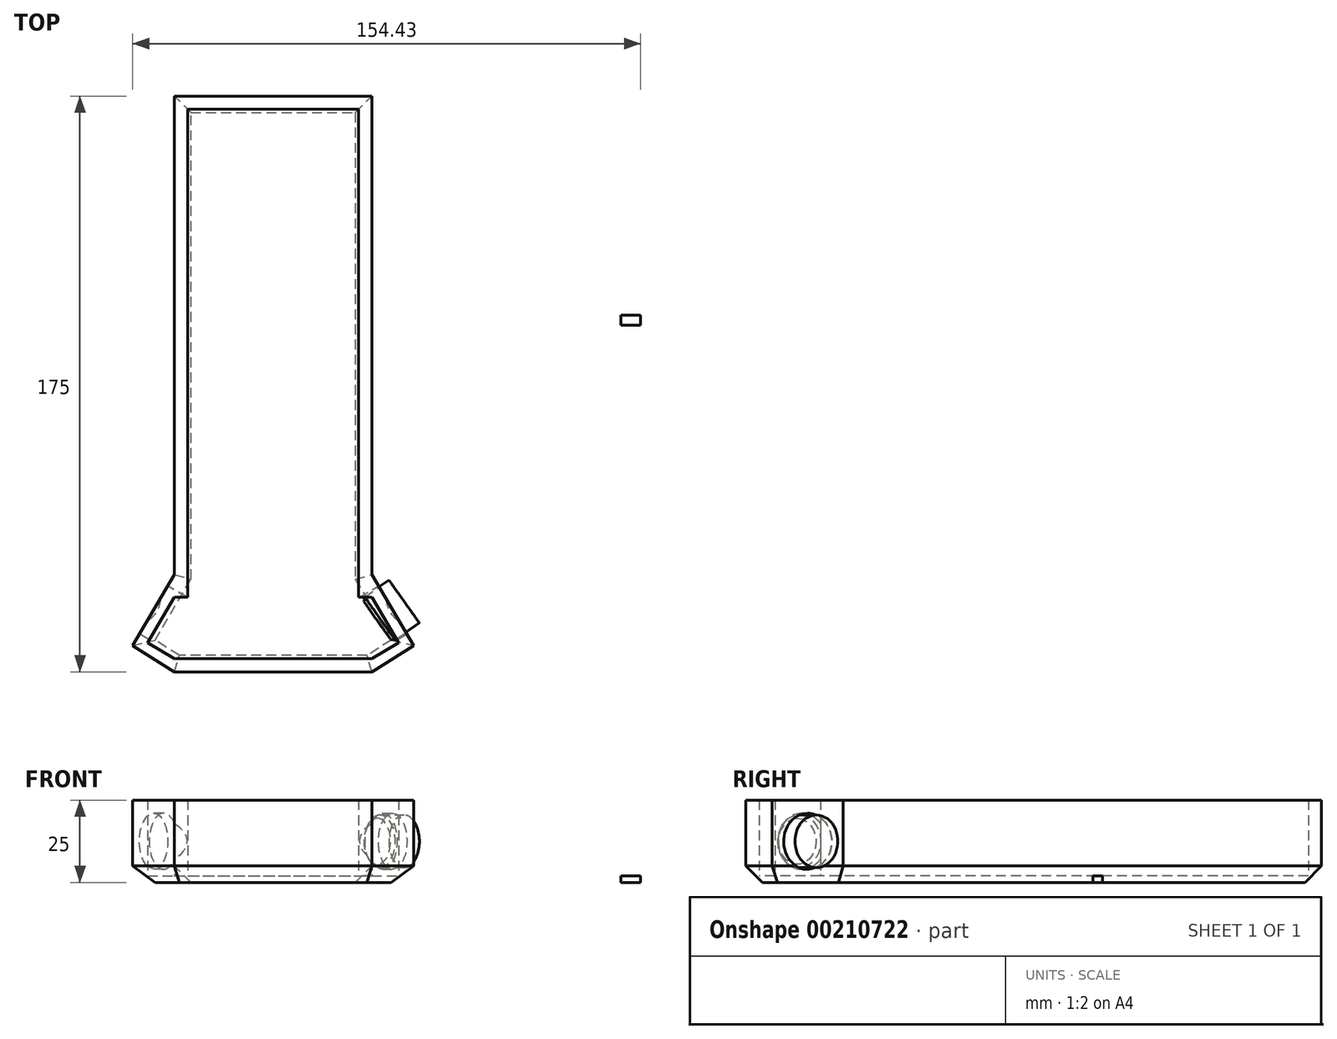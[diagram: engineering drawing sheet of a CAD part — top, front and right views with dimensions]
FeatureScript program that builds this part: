
annotation { "Feature Type Name" : "Feature", "Feature Type Description" : "" }
export const myFeature = defineFeature(function(context is Context, id is Id, definition is map)
    precondition{}
    {
        {
            var Q0;
            Q0=qCreatedBy(makeId("Top.planeOp"),FACE);
            var sketch = newSketch(context, id + "F0", { "sketchPlane" : qUnion([Q0])});
            skLineSegment(sketch, "E0.top", {"start": v(-60, -53.6) * mm, "end": v(0, -53.6) * mm});
            skLineSegment(sketch, "E0.left", {"start": v(-60, 121.4) * mm, "end": v(-60, -30.92) * mm});
            skLineSegment(sketch, "E0.right", {"start": v(0, 121.4) * mm, "end": v(0, -30.92) * mm});
            skLineSegment(sketch, "E1", {"start": v(-60, 121.4) * mm, "end": v(0, 121.4) * mm});
            skLineSegment(sketch, "E2.bottom", {"start": v(-56, 117.4) * mm, "end": v(-4, 117.4) * mm});
            skLineSegment(sketch, "E2.top", {"start": v(-56, -49.6) * mm, "end": v(-4, -49.6) * mm});
            skLineSegment(sketch, "E2.left", {"start": v(-56, 117.4) * mm, "end": v(-56, -30.92) * mm});
            skLineSegment(sketch, "E2.right", {"start": v(-4, 117.4) * mm, "end": v(-4, -30.92) * mm});
            skLineSegment(sketch, "E3", {"start": v(0, -53.6) * mm, "end": v(12.7, -45.6) * mm});
            skLineSegment(sketch, "E4", {"start": v(12.7, -45.6) * mm, "end": v(0, -24.06) * mm});
            skLineSegment(sketch, "E5", {"start": v(11.17, -43.01) * mm, "end": v(0, -49.6) * mm});
            skPoint(sketch, "E5.endSnap0", {"position": v(6.35, -49.6) * mm});
            skLineSegment(sketch, "E6", {"start": v(-4, -49.6) * mm, "end": v(0, -49.6) * mm});
            skLineSegment(sketch, "E7", {"start": v(3, -29.15) * mm, "end": v(0, -30.92) * mm});
            skLineSegment(sketch, "E8", {"start": v(0, -30.92) * mm, "end": v(-4, -30.92) * mm});
            skPoint(sketch, "E9.MirrorCS.end.orphan", {"position": v(-60, -24.06) * mm});
            skPoint(sketch, "E9.MirrorCS.start.orphan", {"position": v(-72.7, -45.6) * mm});
            skPoint(sketch, "E10.MirrorCS.start.orphan", {"position": v(-60, -53.6) * mm});
            skPoint(sketch, "E11.end.orphan", {"position": v(-30, -49.6) * mm});
            skPoint(sketch, "E11.start.orphan", {"position": v(-30, 117.4) * mm});
            skCircle(sketch, "E12", {"center": v(130.43, 55.25) * mm, "radius": 8 * mm});
            skLineSegment(sketch, "E13", {"start": v(138.43, 55.25) * mm, "end": v(122.43, 55.25) * mm});
            skLineSegment(sketch, "E14.MirrorCS", {"start": v(-63, -29.15) * mm, "end": v(-60, -30.92) * mm});
            skLineSegment(sketch, "E15.MirrorCS", {"start": v(-72.7, -45.6) * mm, "end": v(-60, -24.06) * mm});
            skLineSegment(sketch, "E16.MirrorCS", {"start": v(-71.17, -43.01) * mm, "end": v(-60, -49.6) * mm});
            skLineSegment(sketch, "E17.MirrorCS", {"start": v(-60, -53.6) * mm, "end": v(-72.7, -45.6) * mm});
            skLineSegment(sketch, "E18.MirrorCS", {"start": v(-60, -30.92) * mm, "end": v(-56, -30.92) * mm});
            skLineSegment(sketch, "E19.trimOffspring", {"start": v(0, -49.6) * mm, "end": v(0, -53.6) * mm});
            skLineSegment(sketch, "E20", {"start": v(-60, -49.6) * mm, "end": v(-56, -49.6) * mm});
            skLineSegment(sketch, "E21.trimOffspring", {"start": v(-60, -49.6) * mm, "end": v(-60, -53.6) * mm});
            skLineSegment(sketch, "E22", {"start": v(-60, -30.92) * mm, "end": v(-68.17, -44.78) * mm});
            skLineSegment(sketch, "E23", {"start": v(0, -30.92) * mm, "end": v(8.17, -44.78) * mm});
            skLineSegment(sketch, "E24", {"start": v(-60, -30.92) * mm, "end": v(-60, -49.6) * mm});
            skLineSegment(sketch, "E25", {"start": v(-56, -49.6) * mm, "end": v(-56, -30.92) * mm});
            skLineSegment(sketch, "E26", {"start": v(-4, -49.6) * mm, "end": v(-4, -30.92) * mm});
            skLineSegment(sketch, "E27", {"start": v(0, -49.6) * mm, "end": v(0, -30.92) * mm});
            skPoint(sketch, "E28.start.orphan", {"position": v(-30, 9.4) * mm});
            skPoint(sketch, "E29.orphan", {"position": v(-60, 165.4) * mm});
            skLineSegment(sketch, "E30.bottom", {"start": v(75.74, 54.83) * mm, "end": v(81.74, 54.83) * mm});
            skLineSegment(sketch, "E30.top", {"start": v(75.74, 51.83) * mm, "end": v(81.74, 51.83) * mm});
            skLineSegment(sketch, "E30.left", {"start": v(75.74, 54.83) * mm, "end": v(75.74, 51.83) * mm});
            skLineSegment(sketch, "E30.right", {"start": v(81.74, 54.83) * mm, "end": v(81.74, 51.83) * mm});
            skSolve(sketch);
        }
        {
            var Q0;
            {var subQ2=sQuery(id+"F0.wireOp",EDGE,"E0.top");Q0=makeQuery(id+"F0.imprint","IMPRINT",FACE,{"disambiguationData":[TD([[makeQuery(id+"F0.imprint","IMPRINT",EDGE,{"derivedFrom":subQ2}),1.0]])]});}
            var Q1;
            {var subQ0=sQuery(id+"F0.wireOp",EDGE,"E17.MirrorCS");Q1=makeQuery(id+"F0.imprint","IMPRINT",FACE,{"disambiguationData":[TD([[makeQuery(id+"F0.imprint","IMPRINT",EDGE,{"derivedFrom":subQ0}),-1.0]])]});}
            var Q2;
            {var subQ0=sQuery(id+"F0.wireOp",EDGE,"E14.MirrorCS");Q2=makeQuery(id+"F0.imprint","IMPRINT",FACE,{"disambiguationData":[TD([[makeQuery(id+"F0.imprint","IMPRINT",EDGE,{"derivedFrom":subQ0}),1.0]])]});}
            var Q3;
            {var subQ0=sQuery(id+"F0.wireOp",EDGE,"E14.MirrorCS");Q3=makeQuery(id+"F0.imprint","IMPRINT",FACE,{"disambiguationData":[TD([[makeQuery(id+"F0.imprint","IMPRINT",EDGE,{"derivedFrom":subQ0}),-1.0]])]});}
            var Q4;
            {var subQ4=sQuery(id+"F0.wireOp",EDGE,"E1");Q4=makeQuery(id+"F0.imprint","IMPRINT",FACE,{"disambiguationData":[TD([[makeQuery(id+"F0.imprint","IMPRINT",EDGE,{"derivedFrom":subQ4}),-1.0]])]});}
            var Q5;
            {var subQ0=sQuery(id+"F0.wireOp",EDGE,"E7");Q5=makeQuery(id+"F0.imprint","IMPRINT",FACE,{"disambiguationData":[TD([[makeQuery(id+"F0.imprint","IMPRINT",EDGE,{"derivedFrom":subQ0}),-1.0]])]});}
            var Q6;
            {var subQ3=sQuery(id+"F0.wireOp",EDGE,"E7");Q6=makeQuery(id+"F0.imprint","IMPRINT",FACE,{"disambiguationData":[TD([[makeQuery(id+"F0.imprint","IMPRINT",EDGE,{"derivedFrom":subQ3}),1.0]])]});}
            var Q7;
            {var subQ5=sQuery(id+"F0.wireOp",EDGE,"E3");Q7=makeQuery(id+"F0.imprint","IMPRINT",FACE,{"disambiguationData":[TD([[makeQuery(id+"F0.imprint","IMPRINT",EDGE,{"derivedFrom":subQ5}),1.0]])]});}
            extrude(context, id + "F1", {"entities" : qUnion([Q0, Q1, Q2, Q3, Q4, Q5, Q6, Q7]), "depth" : 25 * mm});
        }
        {
            var Q0;
            Q0=makeQuery(id+"F0.imprint","IMPRINT",FACE,{"disambiguationData":[TD([[makeQuery(id+"F0.imprint","IMPRINT",EDGE,{"derivedFrom":sQuery(id+"F0.wireOp",EDGE,"E2.bottom")}),-1.0]])]});
            var Q1;
            {var subQ2=sQuery(id+"F0.wireOp",EDGE,"E23");Q1=makeQuery(id+"F0.imprint","IMPRINT",FACE,{"disambiguationData":[TD([[makeQuery(id+"F0.imprint","IMPRINT",EDGE,{"derivedFrom":subQ2}),-1.0]])]});}
            var Q2;
            Q2=makeQuery(id+"F0.imprint","IMPRINT",FACE,{"disambiguationData":[TD([[makeQuery(id+"F0.imprint","IMPRINT",EDGE,{"derivedFrom":sQuery(id+"F0.wireOp",EDGE,"E6")}),1.0]])]});
            var Q3;
            {var subQ2=sQuery(id+"F0.wireOp",EDGE,"E22");Q3=makeQuery(id+"F0.imprint","IMPRINT",FACE,{"disambiguationData":[TD([[makeQuery(id+"F0.imprint","IMPRINT",EDGE,{"derivedFrom":subQ2}),1.0]])]});}
            var Q4;
            Q4=makeQuery(id+"F0.imprint","IMPRINT",FACE,{"disambiguationData":[TD([[makeQuery(id+"F0.imprint","IMPRINT",EDGE,{"derivedFrom":sQuery(id+"F0.wireOp",EDGE,"E18.MirrorCS")}),-1.0]])]});
            extrude(context, id + "F2", {"entities" : qUnion([Q0, Q1, Q2, Q3, Q4]), "operationType" : NewBodyOperationType.ADD, "depth" : 2 * mm});
        }
        {
            var Q0;
            Q0=makeQuery(id+"F1.opExtrude","SWEPT_FACE",FACE,{"disambiguationData":[OSD([sQuery(id+"F0.wireOp",EDGE,"E4")])]});
            var sketch = newSketch(context, id + "F3", { "sketchPlane" : qUnion([Q0])});
            skCircle(sketch, "E31", {"center": v(-33.23, 12.5) * mm, "radius": 8.5 * mm});
            skPoint(sketch, "E31.centerSnap0", {"position": v(-20.73, 12.5) * mm});
            skPoint(sketch, "E31.centerSnap1", {"position": v(-33.23, 0) * mm});
            skLineSegment(sketch, "E32", {"start": v(-33.23, 4) * mm, "end": v(-33.23, 21) * mm});
            skSolve(sketch);
        }
        {
            var Q0;
            Q0 = qSketchRegion(id + "F3", true);
            extrude(context, id + "F4", {"entities" : qUnion([Q0]), "operationType" : NewBodyOperationType.REMOVE, "oppositeDirection" : true, "depth" : 8 * mm});
        }
        {
            var Q0;
            {var subQ0=sQuery(id+"F0.wireOp",EDGE,"E13");Q0=makeQuery(id+"F0.imprint","IMPRINT",FACE,{"disambiguationData":[TD([[makeQuery(id+"F0.imprint","IMPRINT",EDGE,{"derivedFrom":subQ0}),1.0]])]});}
            var Q1;
            {var subQ0=sQuery(id+"F0.wireOp",EDGE,"E13");Q1=makeQuery(id+"F0.imprint","IMPRINT",FACE,{"disambiguationData":[TD([[makeQuery(id+"F0.imprint","IMPRINT",EDGE,{"derivedFrom":subQ0}),-1.0]])]});}
            extrude(context, id + "F5", {"entities" : qUnion([Q0, Q1]), "depth" : 10 * mm});
        }
        {
            var Q0;
            Q0=makeQuery(id+"F5.opExtrude","CAP_EDGE",EDGE,{"disambiguationData":[OSD([sQuery(id+"F0.wireOp",EDGE,"E12")])],"isStart":false});
            chamfer(context, id + "F6", {"entities" : qUnion([Q0]), "width" : 1 * mm, "tangentPropagation" : true});
        }
        {
            var Q0;
            Q0=makeQuery(id+"F0.imprint","IMPRINT",FACE,{"disambiguationData":[TD([[makeQuery(id+"F0.imprint","IMPRINT",EDGE,{"derivedFrom":sQuery(id+"F0.wireOp",EDGE,"E30.bottom")}),-1.0]])]});
            extrude(context, id + "F7", {"entities" : qUnion([Q0]), "depth" : 2 * mm});
        }
        {
            var Q0;
            Q0=makeQuery(id+"F5.opExtrude","SWEPT_BODY",BODY,{"disambiguationData":[OSD([sQuery(id+"F0.wireOp",EDGE,"E12")])]});
            transform(context, id + "F8", {"entities" : qUnion([Q0]), "transformType" : TransformType.TRANSLATION_3D, "dx" : -115.64 * mm, "dy" : -84.23 * mm, "dz" : 0 * mm, "makeCopy" : false});
        }
        {
            var Q0;
            Q0=makeQuery(id+"F5.opExtrude","CAP_FACE",FACE,{"disambiguationData":[OSD([sQuery(id+"F0.wireOp",EDGE,"E12")])],"isStart":true});
            cPlane(context, id + "F9", {"entities" : qUnion([Q0]), "cplaneType" : CPlaneType.OFFSET, "offset" : 4 * mm, "oppositeDirection" : true, "width" : 150 * mm, "height" : 150 * mm});
        }
        {
            var Q0;
            Q0=qCreatedBy(id+"F9.planeOp",FACE);
            var sketch = newSketch(context, id + "F10", { "sketchPlane" : qUnion([Q0])});
            skLineSegment(sketch, "E33", {"start": v(5.53, 28.8) * mm, "end": v(21.1, 28.8) * mm});
            skLineSegment(sketch, "E34", {"start": v(13.3, 19.78) * mm, "end": v(13.3, 38.13) * mm});
            skPoint(sketch, "E34.startSnap0", {"position": v(13.3, 28.8) * mm});
            skSolve(sketch);
        }
        {
            var Q0;
            Q0=makeQuery(id+"F5.opExtrude","SWEPT_BODY",BODY,{"disambiguationData":[OSD([sQuery(id+"F0.wireOp",EDGE,"E12")])]});
            var Q1;
            Q1=sQuery(id+"F10.wireOp",EDGE,"E34");
            transform(context, id + "F11", {"entities" : qUnion([Q0]), "transformType" : TransformType.ROTATION, "transformAxis" : qUnion([Q1]), "angle" : 90 * degree, "makeCopy" : false});
        }
        {
            var Q0;
            Q0=makeQuery(id+"F5.opExtrude","CAP_FACE",FACE,{"disambiguationData":[OSD([sQuery(id+"F0.wireOp",EDGE,"E12")])],"isStart":true});
            cPlane(context, id + "F12", {"entities" : qUnion([Q0]), "cplaneType" : CPlaneType.OFFSET, "offset" : 4 * mm, "oppositeDirection" : true, "width" : 150 * mm, "height" : 150 * mm});
        }
        {
            var Q0;
            Q0=qCreatedBy(id+"F12.planeOp",FACE);
            var sketch = newSketch(context, id + "F13", { "sketchPlane" : qUnion([Q0])});
            skLineSegment(sketch, "E35", {"start": v(-29.07, 14.1) * mm, "end": v(-29.07, -3.4) * mm});
            skSolve(sketch);
        }
        {
            var Q0;
            Q0=makeQuery(id+"F5.opExtrude","SWEPT_BODY",BODY,{"disambiguationData":[OSD([sQuery(id+"F0.wireOp",EDGE,"E12")])]});
            var Q1;
            Q1=sQuery(id+"F13.wireOp",EDGE,"E35");
            transform(context, id + "F14", {"entities" : qUnion([Q0]), "transformType" : TransformType.ROTATION, "transformAxis" : qUnion([Q1]), "angle" : 35.4 * degree, "oppositeDirection" : true, "makeCopy" : false});
        }
        {
            var Q0;
            Q0=makeQuery(id+"F5.opExtrude","SWEPT_BODY",BODY,{"disambiguationData":[OSD([sQuery(id+"F0.wireOp",EDGE,"E12")])]});
            transform(context, id + "F15", {"entities" : qUnion([Q0]), "transformType" : TransformType.TRANSLATION_3D, "dx" : -6.7 * mm, "dy" : -5.5 * mm, "dz" : 7 * mm, "makeCopy" : false});
        }
        {
            var Q0;
            Q0=makeQuery(id+"F1.opExtrude","SWEPT_FACE",FACE,{"disambiguationData":[OSD([sQuery(id+"F0.wireOp",EDGE,"E15.MirrorCS")])]});
            var sketch = newSketch(context, id + "F16", { "sketchPlane" : qUnion([Q0])});
            skLineSegment(sketch, "E36", {"start": v(51.2, 25) * mm, "end": v(57.68, 18.51) * mm});
            skPoint(sketch, "E37", {"position": v(63.7, 12.5) * mm});
            skCircle(sketch, "E38", {"center": v(63.7, 12.5) * mm, "radius": 8.5 * mm});
            skLineSegment(sketch, "E39.trimOffspring", {"start": v(69.7, 6.49) * mm, "end": v(76.2, 0) * mm});
            skLineSegment(sketch, "E40", {"start": v(57.68, 18.51) * mm, "end": v(69.7, 6.49) * mm});
            skSolve(sketch);
        }
        {
            var Q0;
            {var subQ0=sQuery(id+"F16.wireOp",EDGE,"E40");Q0=makeQuery(id+"F16.imprint","IMPRINT",FACE,{"disambiguationData":[TD([[makeQuery(id+"F16.imprint","IMPRINT",EDGE,{"derivedFrom":subQ0}),-1.0]])]});}
            var Q1;
            {var subQ0=sQuery(id+"F16.wireOp",EDGE,"E40");Q1=makeQuery(id+"F16.imprint","IMPRINT",FACE,{"disambiguationData":[TD([[makeQuery(id+"F16.imprint","IMPRINT",EDGE,{"derivedFrom":subQ0}),1.0]])]});}
            extrude(context, id + "F17", {"entities" : qUnion([Q0, Q1]), "operationType" : NewBodyOperationType.REMOVE, "oppositeDirection" : true, "depth" : 8 * mm});
        }
        {
            var Q0;
            Q0=makeQuery(id+"F1.opExtrude","CAP_EDGE",EDGE,{"disambiguationData":[OSD([sQuery(id+"F0.wireOp",EDGE,"E0.top")])],"isStart":true});
            var Q1;
            Q1=makeQuery(id+"F1.opExtrude","CAP_EDGE",EDGE,{"disambiguationData":[OSD([sQuery(id+"F0.wireOp",EDGE,"E17.MirrorCS")])],"isStart":true});
            var Q2;
            Q2=makeQuery(id+"F1.opExtrude","CAP_EDGE",EDGE,{"disambiguationData":[OSD([sQuery(id+"F0.wireOp",EDGE,"E3")])],"isStart":true});
            var Q3;
            Q3=makeQuery(id+"F1.opExtrude","CAP_EDGE",EDGE,{"disambiguationData":[OSD([sQuery(id+"F0.wireOp",EDGE,"E4")])],"isStart":true});
            var Q4;
            Q4=makeQuery(id+"F1.opExtrude","CAP_EDGE",EDGE,{"disambiguationData":[OSD([sQuery(id+"F0.wireOp",EDGE,"E0.right")])],"isStart":true});
            var Q5;
            Q5=makeQuery(id+"F1.opExtrude","CAP_EDGE",EDGE,{"disambiguationData":[OSD([sQuery(id+"F0.wireOp",EDGE,"E1")])],"isStart":true});
            var Q6;
            Q6=makeQuery(id+"F1.opExtrude","CAP_EDGE",EDGE,{"disambiguationData":[OSD([sQuery(id+"F0.wireOp",EDGE,"E0.left")])],"isStart":true});
            var Q7;
            Q7=makeQuery(id+"F1.opExtrude","CAP_EDGE",EDGE,{"disambiguationData":[OSD([sQuery(id+"F0.wireOp",EDGE,"E15.MirrorCS")])],"isStart":true});
            chamfer(context, id + "F18", {"entities" : qUnion([Q0, Q1, Q2, Q3, Q4, Q5, Q6, Q7]), "width" : 5 * mm, "tangentPropagation" : true});
        }
    });
